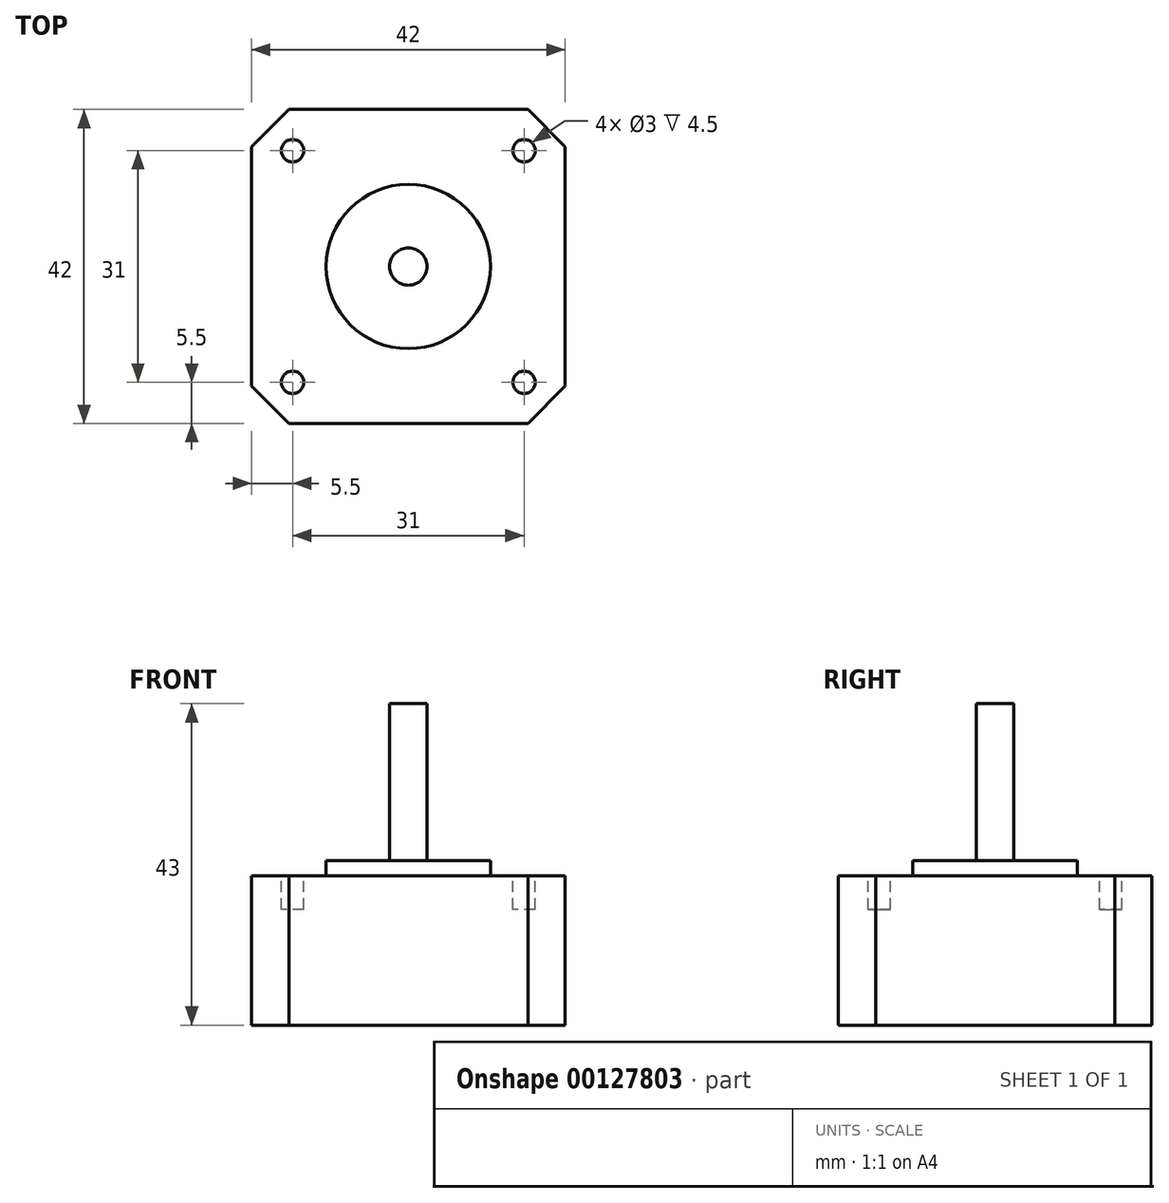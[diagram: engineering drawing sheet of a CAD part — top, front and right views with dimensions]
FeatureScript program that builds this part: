
annotation { "Feature Type Name" : "Feature", "Feature Type Description" : "" }
export const myFeature = defineFeature(function(context is Context, id is Id, definition is map)
    precondition{}
    {
        {
            var Q0;
            Q0=qCreatedBy(makeId("Top.planeOp"),FACE);
            var sketch = newSketch(context, id + "F0", { "sketchPlane" : qUnion([Q0])});
            skLineSegment(sketch, "E0.bottom", {"start": v(21, -21) * mm, "end": v(-21, -21) * mm});
            skLineSegment(sketch, "E0.top", {"start": v(21, 21) * mm, "end": v(-21, 21) * mm});
            skLineSegment(sketch, "E0.left", {"start": v(21, -21) * mm, "end": v(21, 21) * mm});
            skLineSegment(sketch, "E0.right", {"start": v(-21, -21) * mm, "end": v(-21, 21) * mm});
            skPoint(sketch, "E0.middle", {"position": v(0, 0) * mm});
            skSolve(sketch);
        }
        {
            var Q0;
            Q0=makeQuery(id+"F0.imprint","IMPRINT",FACE,{"disambiguationData":[TD([[makeQuery(id+"F0.imprint","IMPRINT",EDGE,{"derivedFrom":sQuery(id+"F0.wireOp",EDGE,"E0.bottom")}),-1.0]])]});
            extrude(context, id + "F1", {"entities" : qUnion([Q0]), "depth" : 20 * mm});
        }
        {
            var Q0;
            Q0=makeQuery(id+"F1.opExtrude","CAP_FACE",FACE,{"disambiguationData":[OSD([sQuery(id+"F0.wireOp",EDGE,"E0.bottom"),sQuery(id+"F0.wireOp",EDGE,"E0.top"),sQuery(id+"F0.wireOp",EDGE,"E0.left"),sQuery(id+"F0.wireOp",EDGE,"E0.right")])],"isStart":false});
            var sketch = newSketch(context, id + "F2", { "sketchPlane" : qUnion([Q0])});
            skCircle(sketch, "E1", {"center": v(0, 0) * mm, "radius": 11 * mm});
            skSolve(sketch);
        }
        {
            var Q0;
            Q0=qSketchRegion(id+"F2",true);
            extrude(context, id + "F3", {"entities" : qUnion([Q0]), "operationType" : NewBodyOperationType.ADD, "depth" : 2 * mm});
        }
        {
            var Q0;
            Q0=makeQuery(id+"F3.opExtrude","CAP_FACE",FACE,{"disambiguationData":[OSD([sQuery(id+"F2.wireOp",EDGE,"E1")])],"isStart":false});
            var sketch = newSketch(context, id + "F4", { "sketchPlane" : qUnion([Q0])});
            skCircle(sketch, "E2", {"center": v(0, 0) * mm, "radius": 2.5 * mm});
            skSolve(sketch);
        }
        {
            var Q0;
            Q0=qSketchRegion(id+"F4",true);
            extrude(context, id + "F5", {"entities" : qUnion([Q0]), "operationType" : NewBodyOperationType.ADD, "depth" : 21 * mm});
        }
        {
            var Q0;
            Q0=makeQuery(id+"F1.opExtrude","CAP_FACE",FACE,{"disambiguationData":[OSD([sQuery(id+"F0.wireOp",EDGE,"E0.bottom"),sQuery(id+"F0.wireOp",EDGE,"E0.top"),sQuery(id+"F0.wireOp",EDGE,"E0.left"),sQuery(id+"F0.wireOp",EDGE,"E0.right")])],"isStart":false});
            var sketch = newSketch(context, id + "F6", { "sketchPlane" : qUnion([Q0])});
            skCircle(sketch, "E3", {"center": v(-15.5, 15.5) * mm, "radius": 1.5 * mm});
            skLineSegment(sketch, "E4", {"start": v(-38.13, 0) * mm, "end": v(0, 0) * mm, "construction": true});
            skLineSegment(sketch, "E5", {"start": v(0, 0) * mm, "end": v(0, 46.17) * mm, "construction": true});
            skCircle(sketch, "E6.MirrorC", {"center": v(-15.5, -15.5) * mm, "radius": 1.5 * mm});
            skCircle(sketch, "E7.MirrorC", {"center": v(15.5, 15.5) * mm, "radius": 1.5 * mm});
            skCircle(sketch, "E8.MirrorC", {"center": v(15.5, -15.5) * mm, "radius": 1.5 * mm});
            skSolve(sketch);
        }
        {
            var Q0;
            Q0=qSketchRegion(id+"F6",true);
            extrude(context, id + "F7", {"entities" : qUnion([Q0]), "operationType" : NewBodyOperationType.REMOVE, "oppositeDirection" : true, "depth" : 4.5 * mm});
        }
        {
            var Q0;
            Q0=makeQuery(id+"F1.opExtrude","SWEPT_EDGE",EDGE,{"disambiguationData":[OSD([sQuery(id+"F0.wireOp",EDGE,"E0.top"),sQuery(id+"F0.wireOp",EDGE,"E0.left")])]});
            var Q1;
            Q1=makeQuery(id+"F1.opExtrude","SWEPT_EDGE",EDGE,{"disambiguationData":[OSD([sQuery(id+"F0.wireOp",EDGE,"E0.bottom"),sQuery(id+"F0.wireOp",EDGE,"E0.left")])]});
            var Q2;
            Q2=makeQuery(id+"F1.opExtrude","SWEPT_EDGE",EDGE,{"disambiguationData":[OSD([sQuery(id+"F0.wireOp",EDGE,"E0.bottom"),sQuery(id+"F0.wireOp",EDGE,"E0.right")])]});
            var Q3;
            Q3=makeQuery(id+"F1.opExtrude","SWEPT_EDGE",EDGE,{"disambiguationData":[OSD([sQuery(id+"F0.wireOp",EDGE,"E0.top"),sQuery(id+"F0.wireOp",EDGE,"E0.right")])]});
            chamfer(context, id + "F8", {"entities" : qUnion([Q0, Q1, Q2, Q3]), "width" : 5 * mm, "tangentPropagation" : true});
        }
    });
